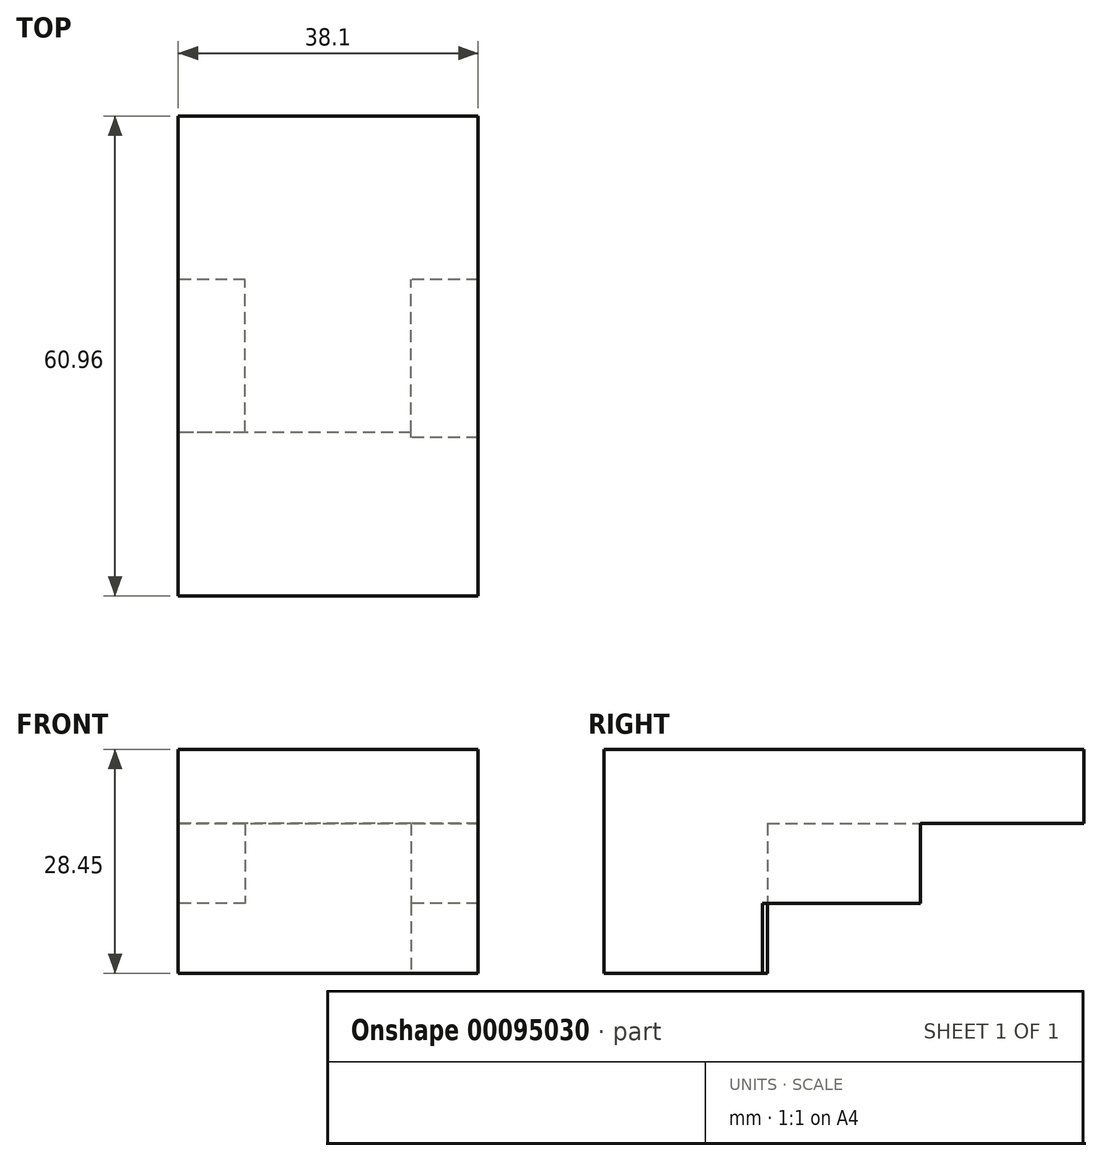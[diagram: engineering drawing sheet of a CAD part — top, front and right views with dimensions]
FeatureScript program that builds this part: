
annotation { "Feature Type Name" : "Feature", "Feature Type Description" : "" }
export const myFeature = defineFeature(function(context is Context, id is Id, definition is map)
    precondition{}
    {
        {
            var Q0;
            Q0=qCreatedBy(makeId("Top.planeOp"),FACE);
            var sketch = newSketch(context, id + "F0", { "sketchPlane" : qUnion([Q0])});
            skLineSegment(sketch, "E0.bottom", {"start": v(-19.05, 30.48) * mm, "end": v(19.05, 30.48) * mm});
            skLineSegment(sketch, "E0.top", {"start": v(-19.05, -30.48) * mm, "end": v(19.05, -30.48) * mm});
            skLineSegment(sketch, "E0.left", {"start": v(-19.05, 30.48) * mm, "end": v(-19.05, -30.48) * mm});
            skLineSegment(sketch, "E0.right", {"start": v(19.05, 30.48) * mm, "end": v(19.05, -30.48) * mm});
            skPoint(sketch, "E0.middle", {"position": v(0, 0) * mm});
            skSolve(sketch);
        }
        {
            var Q0;
            Q0=makeQuery(id+"F0.imprint","IMPRINT",FACE,{"disambiguationData":[TD([[makeQuery(id+"F0.imprint","IMPRINT",EDGE,{"derivedFrom":sQuery(id+"F0.wireOp",EDGE,"E0.bottom")}),-1.0]])]});
            extrude(context, id + "F1", {"entities" : qUnion([Q0]), "depth" : 28.45 * mm});
        }
        {
            var Q0;
            Q0=makeQuery(id+"F1.opExtrude","CAP_FACE",FACE,{"disambiguationData":[OSD([sQuery(id+"F0.wireOp",EDGE,"E0.bottom"),sQuery(id+"F0.wireOp",EDGE,"E0.top"),sQuery(id+"F0.wireOp",EDGE,"E0.left"),sQuery(id+"F0.wireOp",EDGE,"E0.right")])],"isStart":true});
            var sketch = newSketch(context, id + "F2", { "sketchPlane" : qUnion([Q0])});
            skLineSegment(sketch, "E1.bottom", {"start": v(10.53, 9.72) * mm, "end": v(-10.53, 9.72) * mm});
            skLineSegment(sketch, "E1.top", {"start": v(10.53, -9.72) * mm, "end": v(-10.53, -9.72) * mm});
            skLineSegment(sketch, "E1.left", {"start": v(10.53, 9.72) * mm, "end": v(10.53, -9.72) * mm});
            skLineSegment(sketch, "E1.right", {"start": v(-10.53, 9.72) * mm, "end": v(-10.53, -9.72) * mm});
            skPoint(sketch, "E1.middle", {"position": v(0, 0) * mm});
            skLineSegment(sketch, "E2.bottom", {"start": v(19.05, -9.72) * mm, "end": v(-19.05, -9.72) * mm});
            skLineSegment(sketch, "E2.top", {"start": v(19.05, -29.97) * mm, "end": v(-19.05, -29.97) * mm});
            skLineSegment(sketch, "E2.left", {"start": v(19.05, -9.72) * mm, "end": v(19.05, -29.97) * mm});
            skLineSegment(sketch, "E2.right", {"start": v(-19.05, -9.72) * mm, "end": v(-19.05, -29.97) * mm});
            skPoint(sketch, "E2.middle", {"position": v(0, -19.85) * mm});
            skPoint(sketch, "E2.middle.positionSnap0", {"position": v(0, -30.48) * mm});
            skPoint(sketch, "E2.centerSnap0", {"position": v(0, -30.48) * mm});
            skSolve(sketch);
        }
        {
            var Q0;
            Q0=makeQuery(id+"F2.imprint","IMPRINT",FACE,{"disambiguationData":[TD([[makeQuery(id+"F2.imprint","IMPRINT",EDGE,{"derivedFrom":sQuery(id+"F2.wireOp",EDGE,"E1.bottom")}),1.0]])]});
            var Q1;
            Q1=makeQuery(id+"F2.imprint","IMPRINT",FACE,{"disambiguationData":[TD([[makeQuery(id+"F2.imprint","IMPRINT",EDGE,{"derivedFrom":sQuery(id+"F2.wireOp",EDGE,"E2.top")}),-1.0]])]});
            var Q2;
            {var subQ0=sQuery(id+"F2.wireOp",EDGE,"E2.top");Q2=makeQuery(id+"F2.imprint","IMPRINT",FACE,{"disambiguationData":[TD([[makeQuery(id+"F2.imprint","IMPRINT",EDGE,{"derivedFrom":subQ0}),1.0]])]});}
            extrude(context, id + "F3", {"entities" : qUnion([Q0, Q1, Q2]), "operationType" : NewBodyOperationType.REMOVE, "oppositeDirection" : true, "depth" : 19.05 * mm});
        }
        {
            var Q0;
            Q0=makeQuery(id+"F1.opExtrude","CAP_FACE",FACE,{"disambiguationData":[OSD([sQuery(id+"F0.wireOp",EDGE,"E0.bottom"),sQuery(id+"F0.wireOp",EDGE,"E0.top"),sQuery(id+"F0.wireOp",EDGE,"E0.left"),sQuery(id+"F0.wireOp",EDGE,"E0.right")])],"isStart":true});
            var sketch = newSketch(context, id + "F4", { "sketchPlane" : qUnion([Q0])});
            skLineSegment(sketch, "E3.bottom", {"start": v(19.05, 10.38) * mm, "end": v(10.53, 10.38) * mm});
            skLineSegment(sketch, "E3.top", {"start": v(19.05, -9.72) * mm, "end": v(10.53, -9.72) * mm});
            skLineSegment(sketch, "E3.left", {"start": v(19.05, 10.38) * mm, "end": v(19.05, -9.72) * mm});
            skLineSegment(sketch, "E3.right", {"start": v(10.53, 10.38) * mm, "end": v(10.53, -9.72) * mm});
            skLineSegment(sketch, "E4.bottom", {"start": v(-10.53, 9.72) * mm, "end": v(-19.05, 9.72) * mm});
            skLineSegment(sketch, "E4.top", {"start": v(-10.53, -9.72) * mm, "end": v(-19.05, -9.72) * mm});
            skLineSegment(sketch, "E4.left", {"start": v(-10.53, 9.72) * mm, "end": v(-10.53, -9.72) * mm});
            skLineSegment(sketch, "E4.right", {"start": v(-19.05, 9.72) * mm, "end": v(-19.05, -9.72) * mm});
            skSolve(sketch);
        }
        {
            var Q0;
            {var subQ2=sQuery(id+"F4.wireOp",EDGE,"E3.bottom");Q0=makeQuery(id+"F4.imprint","IMPRINT",FACE,{"disambiguationData":[TD([[makeQuery(id+"F4.imprint","IMPRINT",EDGE,{"derivedFrom":subQ2}),1.0]])]});}
            var Q1;
            Q1=makeQuery(id+"F4.imprint","IMPRINT",FACE,{"disambiguationData":[TD([[makeQuery(id+"F4.imprint","IMPRINT",EDGE,{"derivedFrom":sQuery(id+"F4.wireOp",EDGE,"E4.bottom")}),1.0]])]});
            extrude(context, id + "F5", {"entities" : qUnion([Q0, Q1]), "operationType" : NewBodyOperationType.REMOVE, "oppositeDirection" : true, "depth" : 8.9 * mm});
        }
    });
